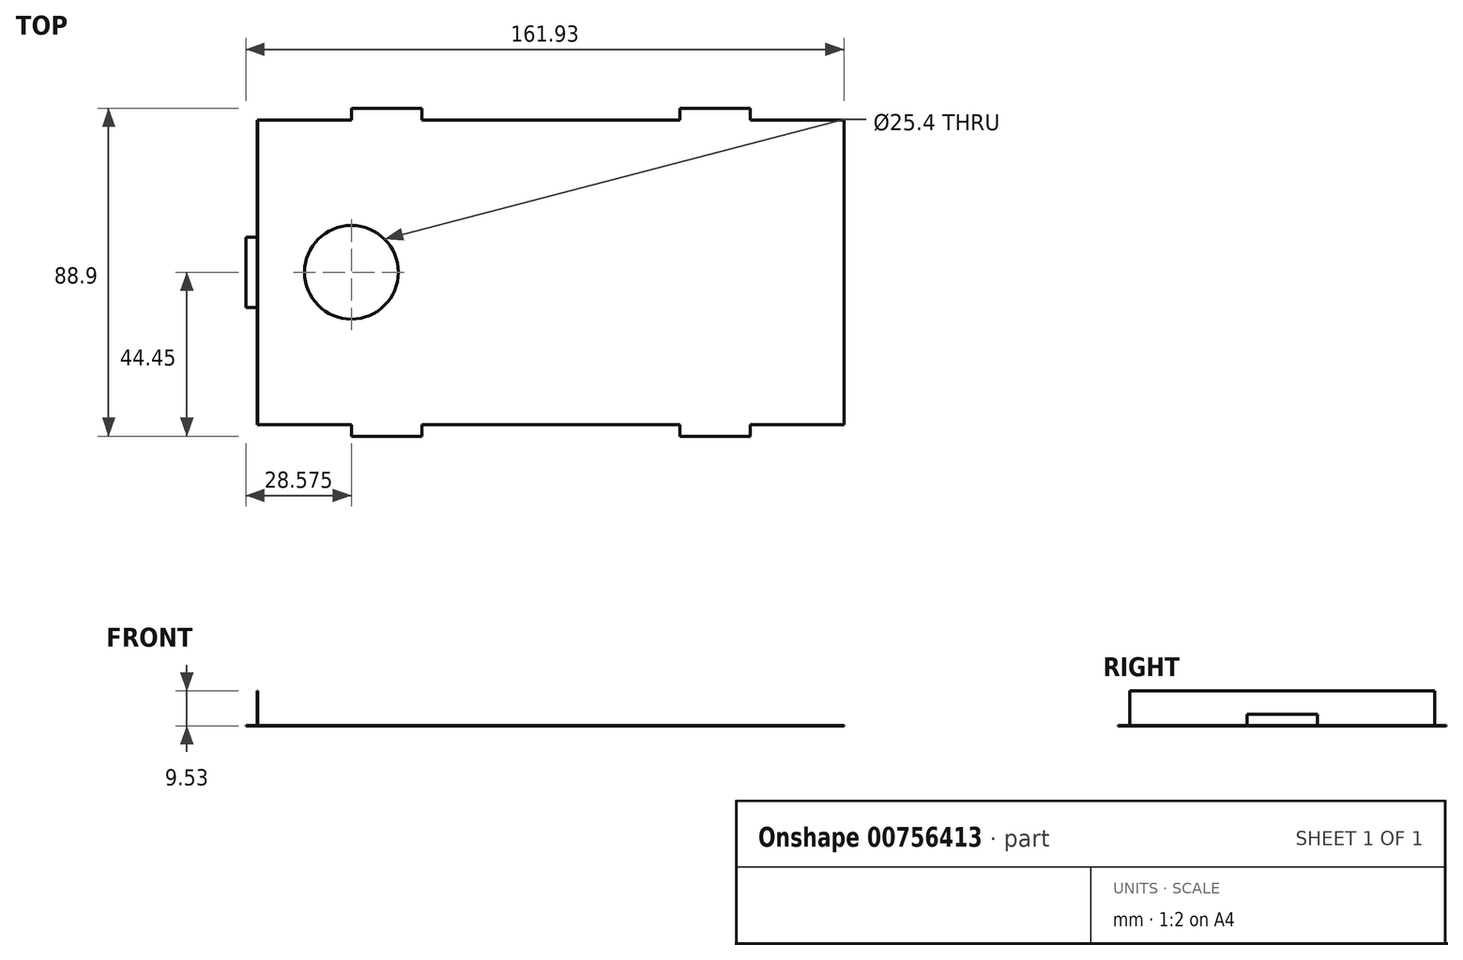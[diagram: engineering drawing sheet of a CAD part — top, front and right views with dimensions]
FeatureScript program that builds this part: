
annotation { "Feature Type Name" : "Feature", "Feature Type Description" : "" }
export const myFeature = defineFeature(function(context is Context, id is Id, definition is map)
    precondition{}
    {
        {
            assignVariable(context, id + "F0", {"name" : "MaterialThickness", "anyValue" : .125});
        }
        {
            var Q0;
            Q0=qCreatedBy(makeId("Top.planeOp"),FACE);
            var sketch = newSketch(context, id + "F1", { "sketchPlane" : qUnion([Q0])});
            skLineSegment(sketch, "E0.bottom", {"start": v(-79.37, 41.28) * mm, "end": v(-53.97, 41.28) * mm});
            skLineSegment(sketch, "E0.top", {"start": v(-79.38, -41.27) * mm, "end": v(-53.97, -41.27) * mm});
            skLineSegment(sketch, "E0.left", {"start": v(-79.37, 41.28) * mm, "end": v(-79.38, 9.52) * mm});
            skLineSegment(sketch, "E0.right", {"start": v(79.38, 41.28) * mm, "end": v(79.38, -41.27) * mm});
            skPoint(sketch, "E0.middle", {"position": v(0, 0) * mm});
            skCircle(sketch, "E1", {"center": v(-53.97, 0) * mm, "radius": 12.7 * mm});
            skLineSegment(sketch, "E2.top", {"start": v(-53.97, 44.45) * mm, "end": v(-34.92, 44.45) * mm});
            skLineSegment(sketch, "E2.left", {"start": v(-53.97, 41.28) * mm, "end": v(-53.97, 44.45) * mm});
            skLineSegment(sketch, "E2.right", {"start": v(-34.92, 41.28) * mm, "end": v(-34.92, 44.45) * mm});
            skLineSegment(sketch, "E3.top", {"start": v(34.93, 44.45) * mm, "end": v(53.98, 44.45) * mm});
            skLineSegment(sketch, "E3.left", {"start": v(34.93, 41.28) * mm, "end": v(34.93, 44.45) * mm});
            skLineSegment(sketch, "E3.right", {"start": v(53.98, 41.28) * mm, "end": v(53.98, 44.45) * mm});
            skLineSegment(sketch, "E4.MirrorCS", {"start": v(34.93, -44.45) * mm, "end": v(53.98, -44.45) * mm});
            skLineSegment(sketch, "E5.MirrorCS", {"start": v(34.93, -41.28) * mm, "end": v(34.93, -44.45) * mm});
            skLineSegment(sketch, "E6.MirrorCS", {"start": v(53.98, -41.28) * mm, "end": v(53.98, -44.45) * mm});
            skLineSegment(sketch, "E7.MirrorCS", {"start": v(-53.97, -41.28) * mm, "end": v(-53.97, -44.45) * mm});
            skLineSegment(sketch, "E8.MirrorCS", {"start": v(-34.92, -41.28) * mm, "end": v(-34.92, -44.45) * mm});
            skLineSegment(sketch, "E9.MirrorCS", {"start": v(-53.97, -44.45) * mm, "end": v(-34.92, -44.45) * mm});
            skLineSegment(sketch, "E10.trimOffspring", {"start": v(53.98, 41.28) * mm, "end": v(79.38, 41.28) * mm});
            skLineSegment(sketch, "E11.trimOffspring", {"start": v(-34.92, 41.28) * mm, "end": v(34.93, 41.28) * mm});
            skLineSegment(sketch, "E12.trimOffspring", {"start": v(-34.92, -41.27) * mm, "end": v(34.93, -41.27) * mm});
            skLineSegment(sketch, "E13.trimOffspring", {"start": v(53.98, -41.27) * mm, "end": v(79.38, -41.27) * mm});
            skLineSegment(sketch, "E14.top", {"start": v(-79.38, -9.52) * mm, "end": v(-82.55, -9.52) * mm});
            skLineSegment(sketch, "E14.right", {"start": v(-82.55, 0) * mm, "end": v(-82.55, -9.52) * mm});
            skLineSegment(sketch, "E15.MirrorCS", {"start": v(-79.38, 9.52) * mm, "end": v(-82.55, 9.52) * mm});
            skLineSegment(sketch, "E16.MirrorCS", {"start": v(-82.55, 0) * mm, "end": v(-82.55, 9.52) * mm});
            skLineSegment(sketch, "E17.trimOffspring", {"start": v(-79.38, -9.52) * mm, "end": v(-79.38, -41.27) * mm});
            skPoint(sketch, "E14.bottom.start.orphan", {"position": v(-79.38, 0) * mm});
            skSolve(sketch);
        }
        {
            var Q0;
            Q0=makeQuery(id+"F1.imprint","IMPRINT",FACE,{"disambiguationData":[TD([[makeQuery(id+"F1.imprint","IMPRINT",EDGE,{"derivedFrom":sQuery(id+"F1.wireOp",EDGE,"E0.bottom")}),-1.0]])]});
            extrude(context, id + "F2", {"entities" : qUnion([Q0]), "depth" : (getVariable(context, 'MaterialThickness')) * mm, "offsetDistance" : 25.4 * mm});
        }
        {
            var Q0;
            Q0=makeQuery(id+"F2.opExtrude","SWEPT_FACE",FACE,{"disambiguationData":[OSD([sQuery(id+"F1.wireOp",EDGE,"E0.left")])]});
            var sketch = newSketch(context, id + "F3", { "sketchPlane" : qUnion([Q0])});
            skLineSegment(sketch, "E18.bottom", {"start": v(-41.27, 0) * mm, "end": v(41.28, 0) * mm});
            skLineSegment(sketch, "E18.top", {"start": v(-41.27, 9.52) * mm, "end": v(41.28, 9.52) * mm});
            skLineSegment(sketch, "E18.left", {"start": v(-41.27, 0) * mm, "end": v(-41.27, 9.52) * mm});
            skLineSegment(sketch, "E18.right", {"start": v(41.28, 0) * mm, "end": v(41.28, 9.52) * mm});
            skLineSegment(sketch, "E19.bottom", {"start": v(-9.52, 0) * mm, "end": v(9.53, 0) * mm});
            skLineSegment(sketch, "E19.top", {"start": v(-9.52, 3.17) * mm, "end": v(9.53, 3.17) * mm});
            skLineSegment(sketch, "E19.left", {"start": v(-9.52, 0) * mm, "end": v(-9.52, 3.17) * mm});
            skLineSegment(sketch, "E19.right", {"start": v(9.53, 0) * mm, "end": v(9.53, 3.17) * mm});
            skSolve(sketch);
        }
        {
            var Q0;
            {var subQ3=sQuery(id+"F3.wireOp",EDGE,"E18.top");Q0=makeQuery(id+"F3.imprint","IMPRINT",FACE,{"disambiguationData":[TD([[makeQuery(id+"F3.imprint","IMPRINT",EDGE,{"derivedFrom":subQ3}),-1.0]])]});}
            var Q1;
            {var subQ3=sQuery(id+"F3.wireOp",EDGE,"E19.left");Q1=makeQuery(id+"F3.imprint","IMPRINT",FACE,{"disambiguationData":[TD([[makeQuery(id+"F3.imprint","IMPRINT",EDGE,{"derivedFrom":subQ3}),-1.0]])]});}
            extrude(context, id + "F4", {"entities" : qUnion([Q0, Q1]), "depth" : (getVariable(context, 'MaterialThickness')) * mm, "offsetDistance" : 25.4 * mm});
        }
    });
